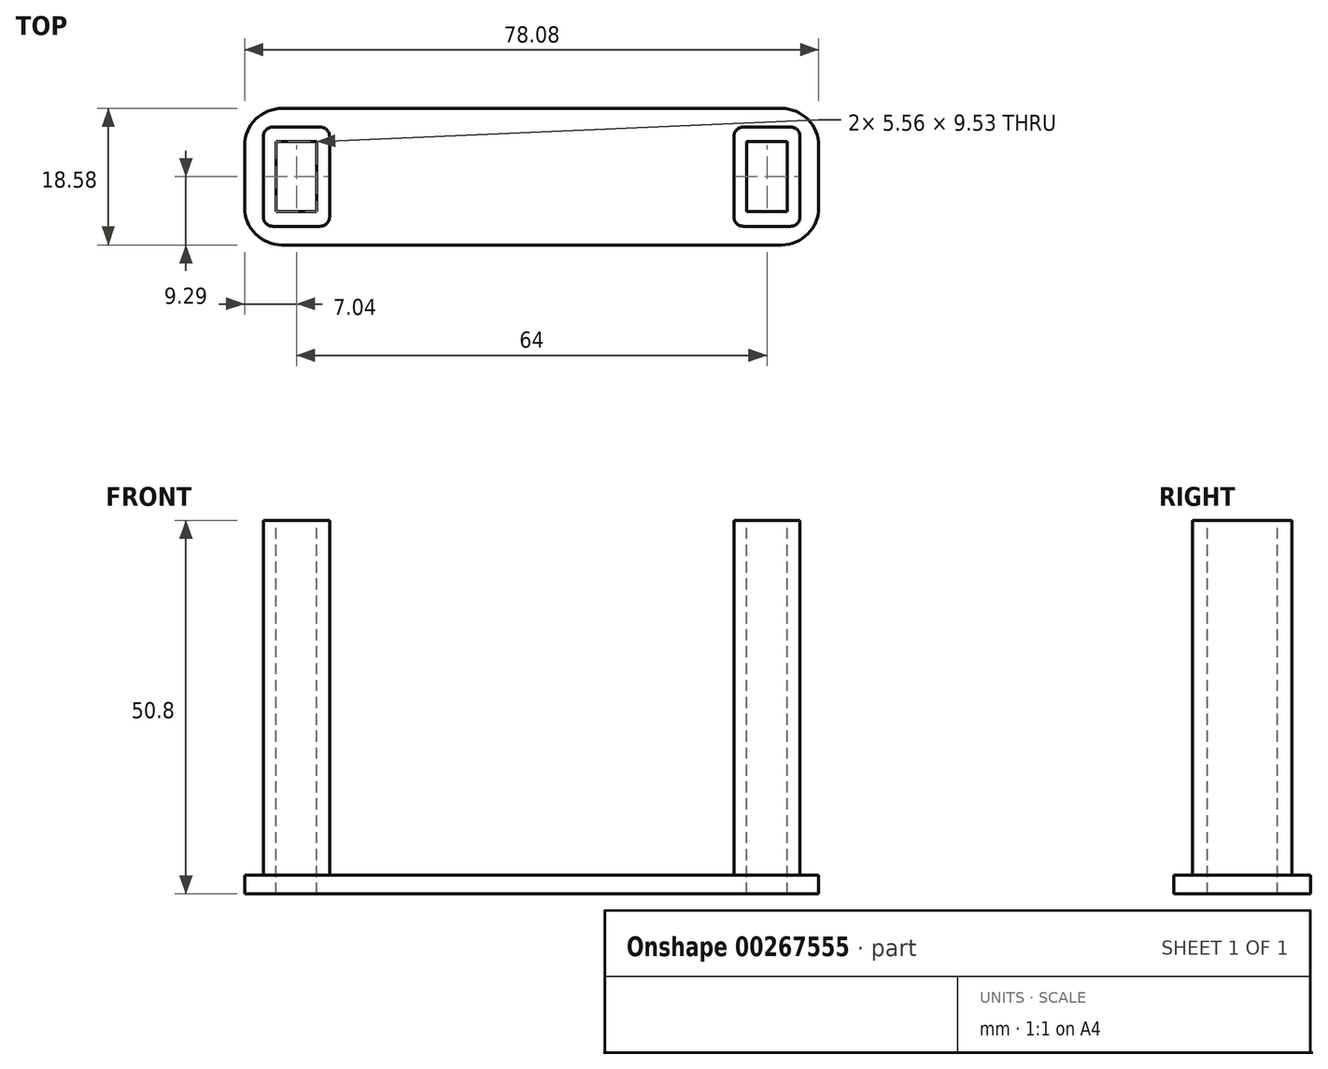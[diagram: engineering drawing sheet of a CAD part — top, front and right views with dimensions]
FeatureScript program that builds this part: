
annotation { "Feature Type Name" : "Feature", "Feature Type Description" : "" }
export const myFeature = defineFeature(function(context is Context, id is Id, definition is map)
    precondition{}
    {
        {
            var Q0;
            Q0=qCreatedBy(makeId("Top.planeOp"),FACE);
            var sketch = newSketch(context, id + "F0", { "sketchPlane" : qUnion([Q0])});
            skLineSegment(sketch, "E0.bottom", {"start": v(39.04, 9.3) * mm, "end": v(-39.04, 9.3) * mm});
            skLineSegment(sketch, "E0.top", {"start": v(39.04, -9.3) * mm, "end": v(-39.04, -9.3) * mm});
            skLineSegment(sketch, "E0.left", {"start": v(39.04, 9.3) * mm, "end": v(39.04, -9.3) * mm});
            skLineSegment(sketch, "E0.right", {"start": v(-39.04, 9.3) * mm, "end": v(-39.04, -9.3) * mm});
            skPoint(sketch, "E0.middle", {"position": v(0, 0) * mm});
            skSolve(sketch);
        }
        {
            var Q0;
            Q0=makeQuery(id+"F0.imprint","IMPRINT",FACE,{"disambiguationData":[TD([[makeQuery(id+"F0.imprint","IMPRINT",EDGE,{"derivedFrom":sQuery(id+"F0.wireOp",EDGE,"E0.bottom")}),1.0]])]});
            extrude(context, id + "F1", {"entities" : qUnion([Q0]), "depth" : 2.54 * mm});
        }
        {
            var Q0;
            Q0=makeQuery(id+"F1.opExtrude","CAP_FACE",FACE,{"disambiguationData":[OSD([sQuery(id+"F0.wireOp",EDGE,"E0.bottom"),sQuery(id+"F0.wireOp",EDGE,"E0.top"),sQuery(id+"F0.wireOp",EDGE,"E0.left"),sQuery(id+"F0.wireOp",EDGE,"E0.right")])],"isStart":false});
            var sketch = newSketch(context, id + "F2", { "sketchPlane" : qUnion([Q0])});
            skLineSegment(sketch, "E1.bottom", {"start": v(36.5, 6.75) * mm, "end": v(27.5, 6.75) * mm});
            skLineSegment(sketch, "E1.top", {"start": v(36.5, -6.75) * mm, "end": v(27.5, -6.75) * mm});
            skLineSegment(sketch, "E1.left", {"start": v(36.5, 6.75) * mm, "end": v(36.5, -6.75) * mm});
            skLineSegment(sketch, "E1.right", {"start": v(27.5, 6.75) * mm, "end": v(27.5, -6.75) * mm});
            skPoint(sketch, "E1.middle", {"position": v(32, 0) * mm});
            skLineSegment(sketch, "E2.bottom", {"start": v(-27.5, 6.75) * mm, "end": v(-36.5, 6.75) * mm});
            skLineSegment(sketch, "E2.top", {"start": v(-27.5, -6.75) * mm, "end": v(-36.5, -6.75) * mm});
            skLineSegment(sketch, "E2.left", {"start": v(-27.5, 6.75) * mm, "end": v(-27.5, -6.75) * mm});
            skLineSegment(sketch, "E2.right", {"start": v(-36.5, 6.75) * mm, "end": v(-36.5, -6.75) * mm});
            skPoint(sketch, "E2.middle", {"position": v(-32, 0) * mm});
            skSolve(sketch);
        }
        {
            var Q0;
            Q0 = qSketchRegion(id + "F2", true);
            extrude(context, id + "F3", {"entities" : qUnion([Q0]), "operationType" : NewBodyOperationType.ADD, "depth" : 48.26 * mm});
        }
        {
            var Q0;
            Q0=makeQuery(id+"F1.opExtrude","SWEPT_EDGE",EDGE,{"disambiguationData":[OSD([sQuery(id+"F0.wireOp",EDGE,"E0.bottom"),sQuery(id+"F0.wireOp",EDGE,"E0.left")])]});
            var Q1;
            Q1=makeQuery(id+"F1.opExtrude","SWEPT_EDGE",EDGE,{"disambiguationData":[OSD([sQuery(id+"F0.wireOp",EDGE,"E0.top"),sQuery(id+"F0.wireOp",EDGE,"E0.left")])]});
            var Q2;
            Q2=makeQuery(id+"F1.opExtrude","SWEPT_EDGE",EDGE,{"disambiguationData":[OSD([sQuery(id+"F0.wireOp",EDGE,"E0.top"),sQuery(id+"F0.wireOp",EDGE,"E0.right")])]});
            var Q3;
            Q3=makeQuery(id+"F1.opExtrude","SWEPT_EDGE",EDGE,{"disambiguationData":[OSD([sQuery(id+"F0.wireOp",EDGE,"E0.bottom"),sQuery(id+"F0.wireOp",EDGE,"E0.right")])]});
            fillet(context, id + "F4", {"entities" : qUnion([Q0, Q1, Q2, Q3]), "radius" : 5.08 * mm, "tangentPropagation" : true, "allowEdgeOverflow" : false});
        }
        {
            var Q0;
            Q0=makeQuery(id+"F3.opExtrude","SWEPT_EDGE",EDGE,{"disambiguationData":[OSD([sQuery(id+"F2.wireOp",EDGE,"E1.bottom"),sQuery(id+"F2.wireOp",EDGE,"E1.left")])]});
            var Q1;
            Q1=makeQuery(id+"F3.opExtrude","SWEPT_EDGE",EDGE,{"disambiguationData":[OSD([sQuery(id+"F2.wireOp",EDGE,"E1.top"),sQuery(id+"F2.wireOp",EDGE,"E1.left")])]});
            var Q2;
            Q2=makeQuery(id+"F3.opExtrude","SWEPT_EDGE",EDGE,{"disambiguationData":[OSD([sQuery(id+"F2.wireOp",EDGE,"E1.top"),sQuery(id+"F2.wireOp",EDGE,"E1.right")])]});
            var Q3;
            Q3=makeQuery(id+"F3.opExtrude","SWEPT_EDGE",EDGE,{"disambiguationData":[OSD([sQuery(id+"F2.wireOp",EDGE,"E1.bottom"),sQuery(id+"F2.wireOp",EDGE,"E1.right")])]});
            var Q4;
            Q4=makeQuery(id+"F3.opExtrude","SWEPT_EDGE",EDGE,{"disambiguationData":[OSD([sQuery(id+"F2.wireOp",EDGE,"E2.top"),sQuery(id+"F2.wireOp",EDGE,"E2.left")])]});
            var Q5;
            Q5=makeQuery(id+"F3.opExtrude","SWEPT_EDGE",EDGE,{"disambiguationData":[OSD([sQuery(id+"F2.wireOp",EDGE,"E2.top"),sQuery(id+"F2.wireOp",EDGE,"E2.right")])]});
            var Q6;
            Q6=makeQuery(id+"F3.opExtrude","SWEPT_EDGE",EDGE,{"disambiguationData":[OSD([sQuery(id+"F2.wireOp",EDGE,"E2.bottom"),sQuery(id+"F2.wireOp",EDGE,"E2.right")])]});
            var Q7;
            Q7=makeQuery(id+"F3.opExtrude","SWEPT_EDGE",EDGE,{"disambiguationData":[OSD([sQuery(id+"F2.wireOp",EDGE,"E2.bottom"),sQuery(id+"F2.wireOp",EDGE,"E2.left")])]});
            fillet(context, id + "F5", {"entities" : qUnion([Q0, Q1, Q2, Q3, Q4, Q5, Q6, Q7]), "radius" : 1.27 * mm, "tangentPropagation" : true, "allowEdgeOverflow" : false});
        }
        {
            var Q0;
            Q0=makeQuery(id+"F3.opExtrude","CAP_FACE",FACE,{"disambiguationData":[OSD([sQuery(id+"F2.wireOp",EDGE,"E1.bottom"),sQuery(id+"F2.wireOp",EDGE,"E1.top"),sQuery(id+"F2.wireOp",EDGE,"E1.left"),sQuery(id+"F2.wireOp",EDGE,"E1.right")])],"isStart":false});
            var sketch = newSketch(context, id + "F6", { "sketchPlane" : qUnion([Q0])});
            skLineSegment(sketch, "E3.bottom", {"start": v(34.78, 4.76) * mm, "end": v(29.22, 4.76) * mm});
            skLineSegment(sketch, "E3.top", {"start": v(34.78, -4.76) * mm, "end": v(29.22, -4.76) * mm});
            skLineSegment(sketch, "E3.left", {"start": v(34.78, 4.76) * mm, "end": v(34.78, -4.76) * mm});
            skLineSegment(sketch, "E3.right", {"start": v(29.22, 4.76) * mm, "end": v(29.22, -4.76) * mm});
            skPoint(sketch, "E3.middle", {"position": v(32, 0) * mm});
            skSolve(sketch);
        }
        {
            var Q0;
            Q0=makeQuery(id+"F6.imprint","IMPRINT",FACE,{"disambiguationData":[TD([[makeQuery(id+"F6.imprint","IMPRINT",EDGE,{"derivedFrom":sQuery(id+"F6.wireOp",EDGE,"E3.bottom")}),1.0]])]});
            extrude(context, id + "F7", {"entities" : qUnion([Q0]), "operationType" : NewBodyOperationType.REMOVE, "oppositeDirection" : true, "depth" : 76.2 * mm});
        }
        {
            var Q0;
            Q0=makeQuery(id+"F3.opExtrude","CAP_FACE",FACE,{"disambiguationData":[OSD([sQuery(id+"F2.wireOp",EDGE,"E2.bottom"),sQuery(id+"F2.wireOp",EDGE,"E2.top"),sQuery(id+"F2.wireOp",EDGE,"E2.left"),sQuery(id+"F2.wireOp",EDGE,"E2.right")])],"isStart":false});
            var sketch = newSketch(context, id + "F8", { "sketchPlane" : qUnion([Q0])});
            skLineSegment(sketch, "E4.bottom", {"start": v(-29.22, 4.76) * mm, "end": v(-34.78, 4.76) * mm});
            skLineSegment(sketch, "E4.top", {"start": v(-29.22, -4.76) * mm, "end": v(-34.78, -4.76) * mm});
            skLineSegment(sketch, "E4.left", {"start": v(-29.22, 4.76) * mm, "end": v(-29.22, -4.76) * mm});
            skLineSegment(sketch, "E4.right", {"start": v(-34.78, 4.76) * mm, "end": v(-34.78, -4.76) * mm});
            skPoint(sketch, "E4.middle", {"position": v(-32, 0) * mm});
            skSolve(sketch);
        }
        {
            var Q0;
            Q0=makeQuery(id+"F8.imprint","IMPRINT",FACE,{"disambiguationData":[TD([[makeQuery(id+"F8.imprint","IMPRINT",EDGE,{"derivedFrom":sQuery(id+"F8.wireOp",EDGE,"E4.bottom")}),1.0]])]});
            extrude(context, id + "F9", {"entities" : qUnion([Q0]), "operationType" : NewBodyOperationType.REMOVE, "oppositeDirection" : true, "depth" : 76.2 * mm});
        }
    });
